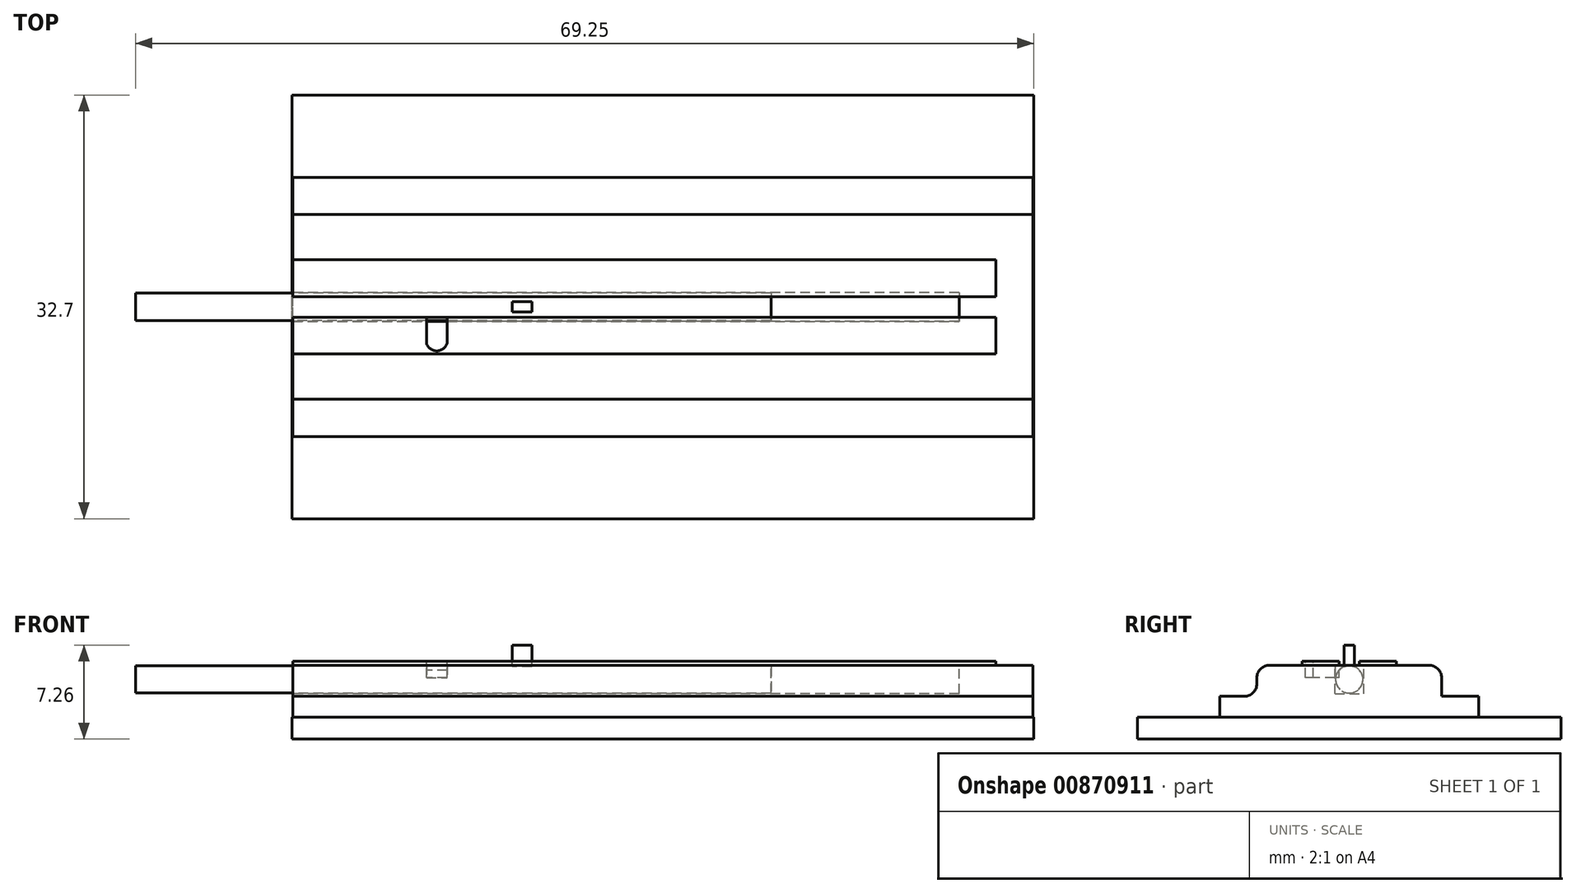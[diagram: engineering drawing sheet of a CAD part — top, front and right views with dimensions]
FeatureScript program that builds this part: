
annotation { "Feature Type Name" : "Feature", "Feature Type Description" : "" }
export const myFeature = defineFeature(function(context is Context, id is Id, definition is map)
    precondition{}
    {
        {
            var Q0;
            Q0=qCreatedBy(makeId("Top.planeOp"),FACE);
            var sketch = newSketch(context, id + "F0", { "sketchPlane" : qUnion([Q0])});
            skLineSegment(sketch, "E0.bottom", {"start": v(28.55, -10) * mm, "end": v(-28.55, -10) * mm});
            skLineSegment(sketch, "E0.top", {"start": v(28.55, 10) * mm, "end": v(-28.55, 10) * mm});
            skLineSegment(sketch, "E0.left", {"start": v(28.55, -10) * mm, "end": v(28.55, 10) * mm});
            skLineSegment(sketch, "E0.right", {"start": v(-28.55, -10) * mm, "end": v(-28.55, 10) * mm});
            skPoint(sketch, "E0.middle", {"position": v(0, 0) * mm});
            skSolve(sketch);
        }
        {
            var Q0;
            Q0=makeQuery(id+"F0.imprint","IMPRINT",FACE,{"disambiguationData":[TD([[makeQuery(id+"F0.imprint","IMPRINT",EDGE,{"derivedFrom":sQuery(id+"F0.wireOp",EDGE,"E0.bottom")}),-1.0]])]});
            extrude(context, id + "F1", {"entities" : qUnion([Q0]), "depth" : 3.3 * mm, "offsetDistance" : 25 * mm});
        }
        {
            var Q0;
            Q0=makeQuery(id+"F1.opExtrude","CAP_FACE",FACE,{"disambiguationData":[OSD([sQuery(id+"F0.wireOp",EDGE,"E0.bottom"),sQuery(id+"F0.wireOp",EDGE,"E0.top"),sQuery(id+"F0.wireOp",EDGE,"E0.left"),sQuery(id+"F0.wireOp",EDGE,"E0.right")])],"isStart":false});
            var sketch = newSketch(context, id + "F2", { "sketchPlane" : qUnion([Q0])});
            skLineSegment(sketch, "E1.bottom", {"start": v(28.55, -7.13) * mm, "end": v(-28.55, -7.13) * mm});
            skLineSegment(sketch, "E1.top", {"start": v(28.55, 7.13) * mm, "end": v(-28.55, 7.13) * mm});
            skLineSegment(sketch, "E1.left", {"start": v(28.55, -7.13) * mm, "end": v(28.55, 7.13) * mm});
            skLineSegment(sketch, "E1.right", {"start": v(-28.55, -7.13) * mm, "end": v(-28.55, 7.13) * mm});
            skPoint(sketch, "E1.middle", {"position": v(0, 0) * mm});
            skSolve(sketch);
        }
        {
            var Q0;
            Q0=makeQuery(id+"F2.imprint","IMPRINT",FACE,{"disambiguationData":[TD([[makeQuery(id+"F2.imprint","IMPRINT",EDGE,{"derivedFrom":sQuery(id+"F2.wireOp",EDGE,"E1.bottom")}),-1.0]])]});
            extrude(context, id + "F3", {"entities" : qUnion([Q0]), "operationType" : NewBodyOperationType.ADD, "depth" : 2.4 * mm, "offsetDistance" : 25 * mm});
        }
        {
            var Q0;
            Q0=makeQuery(id+"F3.opExtrude","CAP_EDGE",EDGE,{"disambiguationData":[OSD([sQuery(id+"F2.wireOp",EDGE,"E1.bottom")])],"isStart":true});
            var Q1;
            Q1=makeQuery(id+"F3.opExtrude","CAP_EDGE",EDGE,{"disambiguationData":[OSD([sQuery(id+"F2.wireOp",EDGE,"E1.top")])],"isStart":true});
            var Q2;
            Q2=makeQuery(id+"F3.opExtrude","CAP_EDGE",EDGE,{"disambiguationData":[OSD([sQuery(id+"F2.wireOp",EDGE,"E1.top")])],"isStart":false});
            var Q3;
            Q3=makeQuery(id+"F3.opExtrude","CAP_EDGE",EDGE,{"disambiguationData":[OSD([sQuery(id+"F2.wireOp",EDGE,"E1.bottom")])],"isStart":false});
            fillet(context, id + "F4", {"entities" : qUnion([Q0, Q1, Q2, Q3]), "radius" : 0.98 * mm, "tangentPropagation" : true, "allowEdgeOverflow" : false});
        }
        {
            var Q0;
            Q0=makeQuery(id+"F3.boolean.opBoolean","MERGE",FACE,{"derivedFrom":[makeQuery(id+"F1.opExtrude","SWEPT_FACE",FACE,{"disambiguationData":[OSD([sQuery(id+"F0.wireOp",EDGE,"E0.right")])]}),makeQuery(id+"F3.opExtrude","SWEPT_FACE",FACE,{"disambiguationData":[OSD([sQuery(id+"F2.wireOp",EDGE,"E1.right")])]})]});
            var sketch = newSketch(context, id + "F5", { "sketchPlane" : qUnion([Q0])});
            skLineSegment(sketch, "E2.bottom", {"start": v(1.11, 3.52) * mm, "end": v(-1.11, 3.52) * mm});
            skLineSegment(sketch, "E2.top", {"start": v(1.11, 7.88) * mm, "end": v(-1.11, 7.88) * mm});
            skLineSegment(sketch, "E2.left", {"start": v(1.11, 3.52) * mm, "end": v(1.11, 7.88) * mm});
            skLineSegment(sketch, "E2.right", {"start": v(-1.11, 3.52) * mm, "end": v(-1.11, 7.88) * mm});
            skPoint(sketch, "E2.middle", {"position": v(0, 5.7) * mm});
            skSolve(sketch);
        }
        {
            var Q0;
            Q0 = qSketchRegion(id + "F5", true);
            extrude(context, id + "F6", {"entities" : qUnion([Q0]), "operationType" : NewBodyOperationType.REMOVE, "oppositeDirection" : true, "depth" : 51.4 * mm, "offsetDistance" : 25 * mm});
        }
        {
            var Q0;
            Q0=makeQuery(id+"F3.opExtrude","CAP_FACE",FACE,{"disambiguationData":[OSD([sQuery(id+"F2.wireOp",EDGE,"E1.bottom"),sQuery(id+"F2.wireOp",EDGE,"E1.top"),sQuery(id+"F2.wireOp",EDGE,"E1.left"),sQuery(id+"F2.wireOp",EDGE,"E1.right")])],"isStart":false});
            var sketch = newSketch(context, id + "F7", { "sketchPlane" : qUnion([Q0])});
            skLineSegment(sketch, "E3.bottom", {"start": v(-28.55, 3.63) * mm, "end": v(25.7, 3.63) * mm});
            skLineSegment(sketch, "E3.top", {"start": v(-28.55, 0.8) * mm, "end": v(25.7, 0.8) * mm});
            skLineSegment(sketch, "E3.left", {"start": v(-28.55, 3.63) * mm, "end": v(-28.55, 0.8) * mm});
            skLineSegment(sketch, "E3.right", {"start": v(25.7, 3.63) * mm, "end": v(25.7, 0.8) * mm});
            skLineSegment(sketch, "E4.MirrorCS", {"start": v(-28.55, -0.8) * mm, "end": v(25.7, -0.8) * mm});
            skLineSegment(sketch, "E5.MirrorCS", {"start": v(25.7, -3.63) * mm, "end": v(25.7, -0.8) * mm});
            skLineSegment(sketch, "E6.MirrorCS", {"start": v(-28.55, -3.63) * mm, "end": v(25.7, -3.63) * mm});
            skLineSegment(sketch, "E7.MirrorCS", {"start": v(-28.55, -3.63) * mm, "end": v(-28.55, -0.8) * mm});
            skSolve(sketch);
        }
        {
            var Q0;
            {var subQ8=sQuery(id+"F7.wireOp",EDGE,"E3.bottom");Q0=makeQuery(id+"F7.imprint","IMPRINT",FACE,{"disambiguationData":[TD([[makeQuery(id+"F7.imprint","IMPRINT",EDGE,{"derivedFrom":subQ8}),-1.0]])]});}
            var Q1;
            {var subQ3=sQuery(id+"F5.wireOp",EDGE,"E2.right");var subQ4=makeQuery(id+"F3.opExtrude","CAP_FACE",FACE,{"disambiguationData":[OSD([sQuery(id+"F2.wireOp",EDGE,"E1.bottom"),sQuery(id+"F2.wireOp",EDGE,"E1.top"),sQuery(id+"F2.wireOp",EDGE,"E1.left"),sQuery(id+"F2.wireOp",EDGE,"E1.right")])],"isStart":false});var subQ7=makeQuery(id+"F6.boolean.opBoolean","INTERSECT",EDGE,{"derivedFrom":[subQ4,makeQuery(id+"F6.opExtrude","SWEPT_FACE",FACE,{"disambiguationData":[OSD([subQ3])]})]});Q1=makeQuery(id+"F7.imprint","IMPRINT",FACE,{"disambiguationData":[TD([[makeQuery(id+"F7.imprint","IMPRINT",EDGE,{"derivedFrom":subQ7}),-1.0]])]});}
            var Q2;
            {var subQ3=sQuery(id+"F5.wireOp",EDGE,"E2.left");var subQ4=makeQuery(id+"F3.opExtrude","CAP_FACE",FACE,{"disambiguationData":[OSD([sQuery(id+"F2.wireOp",EDGE,"E1.bottom"),sQuery(id+"F2.wireOp",EDGE,"E1.top"),sQuery(id+"F2.wireOp",EDGE,"E1.left"),sQuery(id+"F2.wireOp",EDGE,"E1.right")])],"isStart":false});var subQ7=makeQuery(id+"F6.boolean.opBoolean","INTERSECT",EDGE,{"derivedFrom":[subQ4,makeQuery(id+"F6.opExtrude","SWEPT_FACE",FACE,{"disambiguationData":[OSD([subQ3])]})]});Q2=makeQuery(id+"F7.imprint","IMPRINT",FACE,{"disambiguationData":[TD([[makeQuery(id+"F7.imprint","IMPRINT",EDGE,{"derivedFrom":subQ7}),1.0]])]});}
            var Q3;
            {var subQ9=sQuery(id+"F7.wireOp",EDGE,"E5.MirrorCS");Q3=makeQuery(id+"F7.imprint","IMPRINT",FACE,{"disambiguationData":[TD([[makeQuery(id+"F7.imprint","IMPRINT",EDGE,{"derivedFrom":subQ9}),1.0]])]});}
            extrude(context, id + "F8", {"entities" : qUnion([Q0, Q1, Q2, Q3]), "operationType" : NewBodyOperationType.ADD, "depth" : 0.3 * mm, "offsetDistance" : 25 * mm});
        }
        {
            var Q0;
            Q0=makeQuery(id+"F8.boolean.opBoolean","MERGE",FACE,{"derivedFrom":[makeQuery(id+"F3.boolean.opBoolean","MERGE",FACE,{"derivedFrom":[makeQuery(id+"F1.opExtrude","SWEPT_FACE",FACE,{"disambiguationData":[OSD([sQuery(id+"F0.wireOp",EDGE,"E0.right")])]}),makeQuery(id+"F3.opExtrude","SWEPT_FACE",FACE,{"disambiguationData":[OSD([sQuery(id+"F2.wireOp",EDGE,"E1.right")])]})]}),makeQuery(id+"F8.opExtrude","SWEPT_FACE",FACE,{"disambiguationData":[OSD([sQuery(id+"F7.wireOp",EDGE,"E3.left")])]}),makeQuery(id+"F8.opExtrude","SWEPT_FACE",FACE,{"disambiguationData":[OSD([sQuery(id+"F7.wireOp",EDGE,"E7.MirrorCS")])]})]});
            var sketch = newSketch(context, id + "F9", { "sketchPlane" : qUnion([Q0])});
            skCircle(sketch, "E8", {"center": v(0, 4.6) * mm, "radius": 1.06 * mm});
            skPoint(sketch, "E8.centerSnap0", {"position": v(1.11, 4.6) * mm});
            skSolve(sketch);
        }
        {
            var Q0;
            Q0 = qSketchRegion(id + "F9", true);
            extrude(context, id + "F10", {"entities" : qUnion([Q0]), "oppositeDirection" : true, "depth" : 18.45 * mm, "offsetDistance" : 25 * mm});
        }
        {
            var Q0;
            Q0=makeQuery(id+"F10.opExtrude","CAP_FACE",FACE,{"disambiguationData":[OSD([sQuery(id+"F9.wireOp",EDGE,"E8")])],"isStart":false});
            var sketch = newSketch(context, id + "F11", { "sketchPlane" : qUnion([Q0])});
            skLineSegment(sketch, "E9.bottom", {"start": v(0.4, 4.09) * mm, "end": v(-0.4, 4.09) * mm});
            skLineSegment(sketch, "E9.top", {"start": v(0.4, 7.26) * mm, "end": v(-0.4, 7.26) * mm});
            skLineSegment(sketch, "E9.left", {"start": v(0.4, 4.09) * mm, "end": v(0.4, 7.26) * mm});
            skLineSegment(sketch, "E9.right", {"start": v(-0.4, 4.09) * mm, "end": v(-0.4, 7.26) * mm});
            skPoint(sketch, "E9.middle", {"position": v(0, 5.67) * mm});
            skSolve(sketch);
        }
        {
            var Q0;
            Q0 = qSketchRegion(id + "F11", true);
            extrude(context, id + "F12", {"entities" : qUnion([Q0]), "operationType" : NewBodyOperationType.ADD, "oppositeDirection" : true, "depth" : 1.5 * mm, "offsetDistance" : 25 * mm});
        }
        {
            var Q0;
            Q0=makeQuery(id+"F12.boolean.opBoolean","MERGE",FACE,{"derivedFrom":[makeQuery(id+"F10.opExtrude","CAP_FACE",FACE,{"disambiguationData":[OSD([sQuery(id+"F9.wireOp",EDGE,"E8")])],"isStart":false}),makeQuery(id+"F12.opExtrude","CAP_FACE",FACE,{"disambiguationData":[OSD([sQuery(id+"F11.wireOp",EDGE,"E9.bottom"),sQuery(id+"F11.wireOp",EDGE,"E9.top"),sQuery(id+"F11.wireOp",EDGE,"E9.left"),sQuery(id+"F11.wireOp",EDGE,"E9.right")])],"isStart":true})]});
            var sketch = newSketch(context, id + "F13", { "sketchPlane" : qUnion([Q0])});
            skCircle(sketch, "E10", {"center": v(0, 4.6) * mm, "radius": 1.06 * mm});
            skSolve(sketch);
        }
        {
            var Q0;
            Q0 = qSketchRegion(id + "F13", true);
            extrude(context, id + "F14", {"entities" : qUnion([Q0]), "operationType" : NewBodyOperationType.ADD, "depth" : 18.45 * mm, "offsetDistance" : 25 * mm});
        }
        {
            var Q0;
            Q0=makeQuery(id+"F8.opExtrude","CAP_FACE",FACE,{"disambiguationData":[OSD([sQuery(id+"F7.wireOp",EDGE,"E4.MirrorCS"),sQuery(id+"F7.wireOp",EDGE,"E5.MirrorCS"),sQuery(id+"F7.wireOp",EDGE,"E6.MirrorCS"),sQuery(id+"F7.wireOp",EDGE,"E7.MirrorCS")])],"isStart":false});
            var sketch = newSketch(context, id + "F15", { "sketchPlane" : qUnion([Q0])});
            skLineSegment(sketch, "E11.bottom", {"start": v(-18.23, -0.8) * mm, "end": v(-16.63, -0.8) * mm});
            skLineSegment(sketch, "E11.top", {"start": v(-18.23, -2.8) * mm, "end": v(-16.63, -2.8) * mm});
            skLineSegment(sketch, "E11.left", {"start": v(-18.23, -0.8) * mm, "end": v(-18.23, -2.8) * mm});
            skLineSegment(sketch, "E11.right", {"start": v(-16.63, -0.8) * mm, "end": v(-16.63, -2.8) * mm});
            skSolve(sketch);
        }
        {
            var Q0;
            Q0 = qSketchRegion(id + "F15", true);
            extrude(context, id + "F16", {"entities" : qUnion([Q0]), "operationType" : NewBodyOperationType.REMOVE, "oppositeDirection" : true, "depth" : 1.25 * mm, "offsetDistance" : 25 * mm});
        }
        {
            var Q0;
            Q0=makeQuery(id+"F8.opExtrude","CAP_FACE",FACE,{"disambiguationData":[OSD([sQuery(id+"F7.wireOp",EDGE,"E4.MirrorCS"),sQuery(id+"F7.wireOp",EDGE,"E5.MirrorCS"),sQuery(id+"F7.wireOp",EDGE,"E6.MirrorCS"),sQuery(id+"F7.wireOp",EDGE,"E7.MirrorCS")])],"isStart":false});
            var sketch = newSketch(context, id + "F17", { "sketchPlane" : qUnion([Q0])});
            skArc(sketch, "E12", {"start": v(-18.23, -2.8) * mm, "mid": v(-17.43, -3.4) * mm, "end": v(-16.63, -2.8) * mm});
            skSolve(sketch);
        }
        {
            var Q0;
            Q0 = qSketchRegion(id + "F17", true);
            var Q1;
            Q1=makeQuery(id+"F17.imprint","IMPRINT",FACE,{"disambiguationData":[TD([[makeQuery(id+"F17.imprint","IMPRINT",EDGE,{"derivedFrom":sQuery(id+"F17.wireOp",EDGE,"E12")}),1.0]])]});
            extrude(context, id + "F18", {"entities" : qUnion([Q0, Q1]), "operationType" : NewBodyOperationType.REMOVE, "oppositeDirection" : true, "depth" : 1.25 * mm, "offsetDistance" : 25 * mm});
        }
        {
            var Q0;
            Q0=makeQuery(id+"F10.opExtrude","CAP_FACE",FACE,{"disambiguationData":[OSD([sQuery(id+"F9.wireOp",EDGE,"E8")])],"isStart":true});
            var sketch = newSketch(context, id + "F19", { "sketchPlane" : qUnion([Q0])});
            skCircle(sketch, "E13", {"center": v(0, 4.6) * mm, "radius": 1.06 * mm});
            skSolve(sketch);
        }
        {
            var Q0;
            Q0 = qSketchRegion(id + "F19", true);
            extrude(context, id + "F20", {"entities" : qUnion([Q0]), "operationType" : NewBodyOperationType.ADD, "depth" : 12.1 * mm, "offsetDistance" : 25 * mm});
        }
        {
            var Q0;
            Q0=qCreatedBy(makeId("Top.planeOp"),FACE);
            var sketch = newSketch(context, id + "F21", { "sketchPlane" : qUnion([Q0])});
            skLineSegment(sketch, "E14.bottom", {"start": v(28.6, -16.35) * mm, "end": v(-28.6, -16.35) * mm});
            skLineSegment(sketch, "E14.top", {"start": v(28.6, 16.35) * mm, "end": v(-28.6, 16.35) * mm});
            skLineSegment(sketch, "E14.left", {"start": v(28.6, -16.35) * mm, "end": v(28.6, 16.35) * mm});
            skLineSegment(sketch, "E14.right", {"start": v(-28.6, -16.35) * mm, "end": v(-28.6, 16.35) * mm});
            skPoint(sketch, "E14.middle", {"position": v(0, 0) * mm});
            skSolve(sketch);
        }
        {
            var Q0;
            Q0 = qSketchRegion(id + "F21", true);
            extrude(context, id + "F22", {"entities" : qUnion([Q0]), "operationType" : NewBodyOperationType.ADD, "depth" : 1.7 * mm, "offsetDistance" : 25 * mm});
        }
    });
